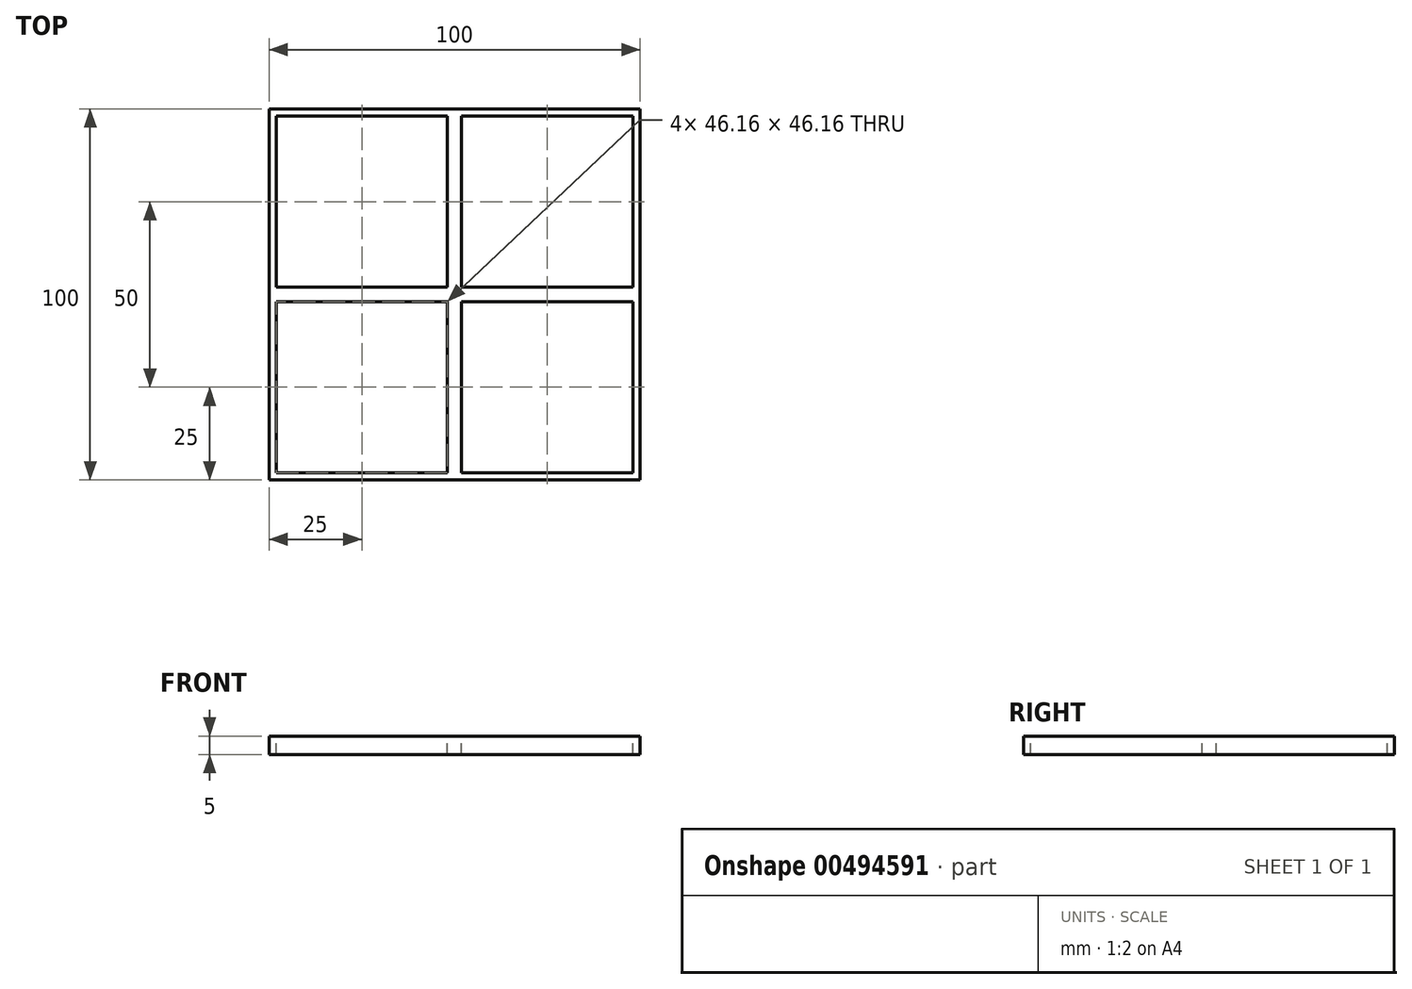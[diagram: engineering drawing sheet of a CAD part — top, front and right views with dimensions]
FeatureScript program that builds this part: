
annotation { "Feature Type Name" : "Feature", "Feature Type Description" : "" }
export const myFeature = defineFeature(function(context is Context, id is Id, definition is map)
    precondition{}
    {
        {
            var Q0;
            Q0=qCreatedBy(makeId("Top.planeOp"),FACE);
            var sketch = newSketch(context, id + "F0", { "sketchPlane" : qUnion([Q0])});
            skLineSegment(sketch, "E0.bottom", {"start": v(50, 50) * mm, "end": v(-50, 50) * mm});
            skLineSegment(sketch, "E0.top", {"start": v(50, -50) * mm, "end": v(-50, -50) * mm});
            skLineSegment(sketch, "E0.left", {"start": v(50, 50) * mm, "end": v(50, -50) * mm});
            skLineSegment(sketch, "E0.right", {"start": v(-50, 50) * mm, "end": v(-50, -50) * mm});
            skPoint(sketch, "E0.middle", {"position": v(0, 0) * mm});
            skSolve(sketch);
        }
        {
            var Q0;
            Q0=makeQuery(id+"F0.imprint","IMPRINT",FACE,{"disambiguationData":[TD([[makeQuery(id+"F0.imprint","IMPRINT",EDGE,{"derivedFrom":sQuery(id+"F0.wireOp",EDGE,"E0.bottom")}),1.0]])]});
            extrude(context, id + "F1", {"entities" : qUnion([Q0]), "depth" : 5 * mm});
        }
        {
            var Q0;
            Q0=makeQuery(id+"F1.opExtrude","CAP_FACE",FACE,{"disambiguationData":[OSD([sQuery(id+"F0.wireOp",EDGE,"E0.bottom"),sQuery(id+"F0.wireOp",EDGE,"E0.top"),sQuery(id+"F0.wireOp",EDGE,"E0.left"),sQuery(id+"F0.wireOp",EDGE,"E0.right")])],"isStart":false});
            var sketch = newSketch(context, id + "F2", { "sketchPlane" : qUnion([Q0])});
            skLineSegment(sketch, "E1.bottom", {"start": v(48.08, 48.08) * mm, "end": v(-48.08, 48.08) * mm, "construction": true});
            skLineSegment(sketch, "E1.top", {"start": v(48.08, -48.08) * mm, "end": v(-48.08, -48.08) * mm, "construction": true});
            skLineSegment(sketch, "E1.left", {"start": v(48.08, 48.08) * mm, "end": v(48.08, -48.08) * mm, "construction": true});
            skLineSegment(sketch, "E1.right", {"start": v(-48.08, 48.08) * mm, "end": v(-48.08, -48.08) * mm, "construction": true});
            skPoint(sketch, "E1.middle", {"position": v(0, 0) * mm});
            skLineSegment(sketch, "E2.bottom", {"start": v(48.08, 48.08) * mm, "end": v(1.92, 48.08) * mm});
            skLineSegment(sketch, "E2.top", {"start": v(48.08, 1.92) * mm, "end": v(1.92, 1.92) * mm});
            skLineSegment(sketch, "E2.left", {"start": v(48.08, 48.08) * mm, "end": v(48.08, 1.92) * mm});
            skLineSegment(sketch, "E2.right", {"start": v(1.92, 48.08) * mm, "end": v(1.92, 1.92) * mm});
            skLineSegment(sketch, "E3.bottom", {"start": v(-48.08, 48.08) * mm, "end": v(-1.92, 48.08) * mm});
            skLineSegment(sketch, "E3.top", {"start": v(-48.08, 1.92) * mm, "end": v(-1.92, 1.92) * mm});
            skLineSegment(sketch, "E3.left", {"start": v(-48.08, 48.08) * mm, "end": v(-48.08, 1.92) * mm});
            skLineSegment(sketch, "E3.right", {"start": v(-1.92, 48.08) * mm, "end": v(-1.92, 1.92) * mm});
            skLineSegment(sketch, "E4.bottom", {"start": v(-48.08, -48.08) * mm, "end": v(-1.92, -48.08) * mm});
            skLineSegment(sketch, "E4.top", {"start": v(-48.08, -1.92) * mm, "end": v(-1.92, -1.92) * mm});
            skLineSegment(sketch, "E4.left", {"start": v(-48.08, -48.08) * mm, "end": v(-48.08, -1.92) * mm});
            skLineSegment(sketch, "E4.right", {"start": v(-1.92, -48.08) * mm, "end": v(-1.92, -1.92) * mm});
            skLineSegment(sketch, "E5.bottom", {"start": v(48.08, -48.08) * mm, "end": v(1.92, -48.08) * mm});
            skLineSegment(sketch, "E5.top", {"start": v(48.08, -1.92) * mm, "end": v(1.92, -1.92) * mm});
            skLineSegment(sketch, "E5.left", {"start": v(48.08, -48.08) * mm, "end": v(48.08, -1.92) * mm});
            skLineSegment(sketch, "E5.right", {"start": v(1.92, -48.08) * mm, "end": v(1.92, -1.92) * mm});
            skSolve(sketch);
        }
        {
            var Q0;
            Q0=makeQuery(id+"F2.imprint","IMPRINT",FACE,{"disambiguationData":[TD([[makeQuery(id+"F2.imprint","IMPRINT",EDGE,{"derivedFrom":sQuery(id+"F2.wireOp",EDGE,"E3.bottom")}),-1.0]])]});
            var Q1;
            Q1=makeQuery(id+"F2.imprint","IMPRINT",FACE,{"disambiguationData":[TD([[makeQuery(id+"F2.imprint","IMPRINT",EDGE,{"derivedFrom":sQuery(id+"F2.wireOp",EDGE,"E2.bottom")}),1.0]])]});
            var Q2;
            Q2=makeQuery(id+"F2.imprint","IMPRINT",FACE,{"disambiguationData":[TD([[makeQuery(id+"F2.imprint","IMPRINT",EDGE,{"derivedFrom":sQuery(id+"F2.wireOp",EDGE,"E5.bottom")}),-1.0]])]});
            var Q3;
            Q3=makeQuery(id+"F2.imprint","IMPRINT",FACE,{"disambiguationData":[TD([[makeQuery(id+"F2.imprint","IMPRINT",EDGE,{"derivedFrom":sQuery(id+"F2.wireOp",EDGE,"E4.bottom")}),1.0]])]});
            extrude(context, id + "F3", {"entities" : qUnion([Q0, Q1, Q2, Q3]), "operationType" : NewBodyOperationType.REMOVE, "endBound" : BoundingType.UP_TO_NEXT, "oppositeDirection" : true, "depth" : 25 * mm});
        }
    });
